# Revit family: Kos Gen 2 - Round
name_source: partatom
category: Lighting Fixtures
revit_build: Autodesk Revit 2018 (Build: 20170223_1515(x64)
units: mm (PartAtom-declared; Revit-internal decimal feet)

## family parameters
Always vertical = Yes
Cut with Voids When Loaded = No
Host = Ceiling
Light Source = No
OmniClass Number = 23.80.70.11
OmniClass Title = Luminaries for Internal Lighting
Part Type = Normal
Room Calculation Point = No
Round Connector Dimension = Use Diameter
Shared = No

## types (4) — shared parameters
Dimmable = Lamp Dependent
Dimming Method = Lamp Dependent
Efficacy (lm/w) = Lamp Dependent
Electrical Class = Class 1
IP Rating = IP65
Lamp = GU 10
Light Source Fixed = No
Main Material = Metal - Aluminium
Power (Watts) = 6 W LED Max
Product Name = Kos Round II
Product Size MM = 85 H X 85 Dia
Wattage Comments = -
Weight KG = 0.3

## per-type parameters (varying)
| type | Main Finish | Product Location | Product SKU | product URL |
| Kos II - Matt White | Matt White | Bathroom/Indoor/Outdoor
Indoor
Outdoor, Indoor, Bathroom | 1326039 | www.astrolighting.com/1326039 |
| Kos II - Textured Black | Textured Black | Bathroom/Indoor/Outdoor | 1326040 | www.astrolighting.com/1326040 |
| Kos II - Textured Grey | Textured Grey | Bathroom/Indoor/Outdoor | 1326041 | www.astrolighting.com/1326041 |
| Kos II - Polished Chrome | Polished Chrome | Bathroom/Indoor
Indoor
Outdoor, Indoor, Bathroom | 1326042 | www.astrolighting.com/1326042 |

## geometry (parser evidence)
native form markers: Sweep x2
no freeform markers — native parametric forms only
